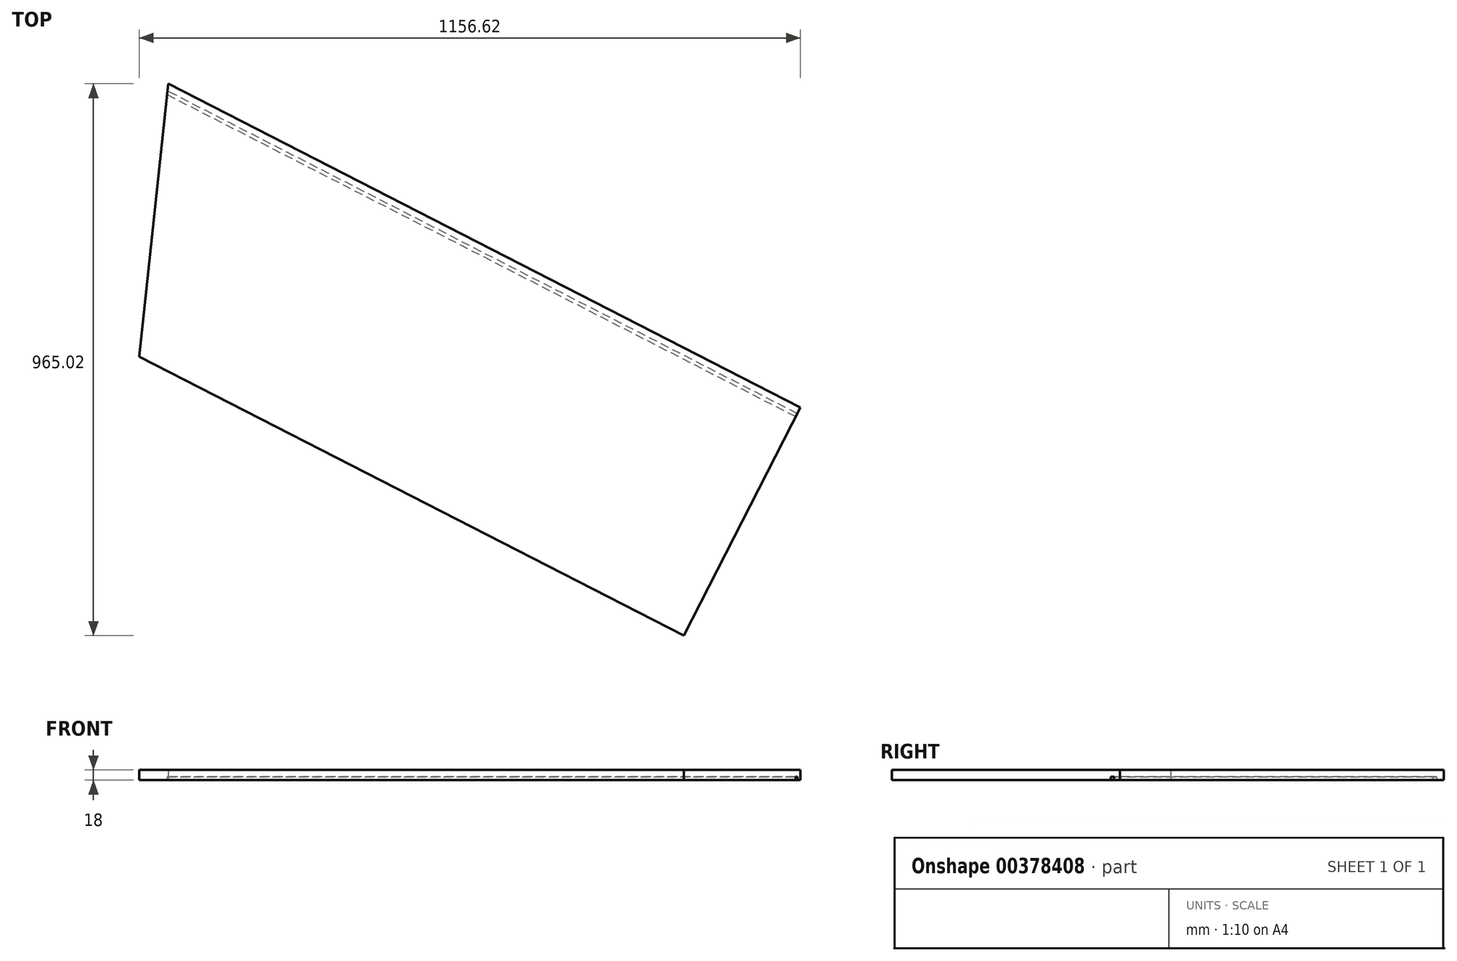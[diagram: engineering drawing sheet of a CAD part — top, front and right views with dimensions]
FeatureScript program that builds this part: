
annotation { "Feature Type Name" : "Feature", "Feature Type Description" : "" }
export const myFeature = defineFeature(function(context is Context, id is Id, definition is map)
    precondition{}
    {
        {
            var Q0;
            Q0=qCreatedBy(makeId("Top.planeOp"),FACE);
            var sketch = newSketch(context, id + "F0", { "sketchPlane" : qUnion([Q0])});
            skLineSegment(sketch, "E0", {"start": v(-270.62, 374.7) * mm, "end": v(834.82, -191.48) * mm});
            skLineSegment(sketch, "E1", {"start": v(834.82, -191.48) * mm, "end": v(630.54, -590.32) * mm});
            skLineSegment(sketch, "E2", {"start": v(630.54, -590.32) * mm, "end": v(-321.8, -102.56) * mm});
            skLineSegment(sketch, "E3", {"start": v(-270.62, 374.7) * mm, "end": v(-321.8, -102.56) * mm});
            skSolve(sketch);
        }
        {
            var Q0;
            Q0=qSketchRegion(id+"F0",true);
            extrude(context, id + "F1", {"entities" : qUnion([Q0]), "depth" : 18 * mm});
        }
        {
            var Q0;
            Q0=makeQuery(id+"F1.opExtrude","CAP_FACE",FACE,{"disambiguationData":[OSD([sQuery(id+"F0.wireOp",EDGE,"hm7g1ifC-j8bG-lpUX-5ii8-XuTQjQwk62bA"),sQuery(id+"F0.wireOp",EDGE,"E0"),sQuery(id+"F0.wireOp",EDGE,"E1"),sQuery(id+"F0.wireOp",EDGE,"E2")])],"isStart":true});
            var sketch = newSketch(context, id + "F2", { "sketchPlane" : qUnion([Q0])});
            skLineSegment(sketch, "E4", {"start": v(829.35, 202.16) * mm, "end": v(-272, -361.92) * mm});
            skLineSegment(sketch, "E5", {"start": v(-272, -361.92) * mm, "end": v(-272.68, -355.53) * mm});
            skLineSegment(sketch, "E6", {"start": v(-272.68, -355.53) * mm, "end": v(826.62, 207.5) * mm});
            skLineSegment(sketch, "E7", {"start": v(826.62, 207.5) * mm, "end": v(829.35, 202.16) * mm});
            skSolve(sketch);
        }
        {
            var Q0;
            Q0=qSketchRegion(id+"F2",true);
            extrude(context, id + "F3", {"entities" : qUnion([Q0]), "operationType" : NewBodyOperationType.REMOVE, "oppositeDirection" : true, "depth" : 6 * mm});
        }
    });
